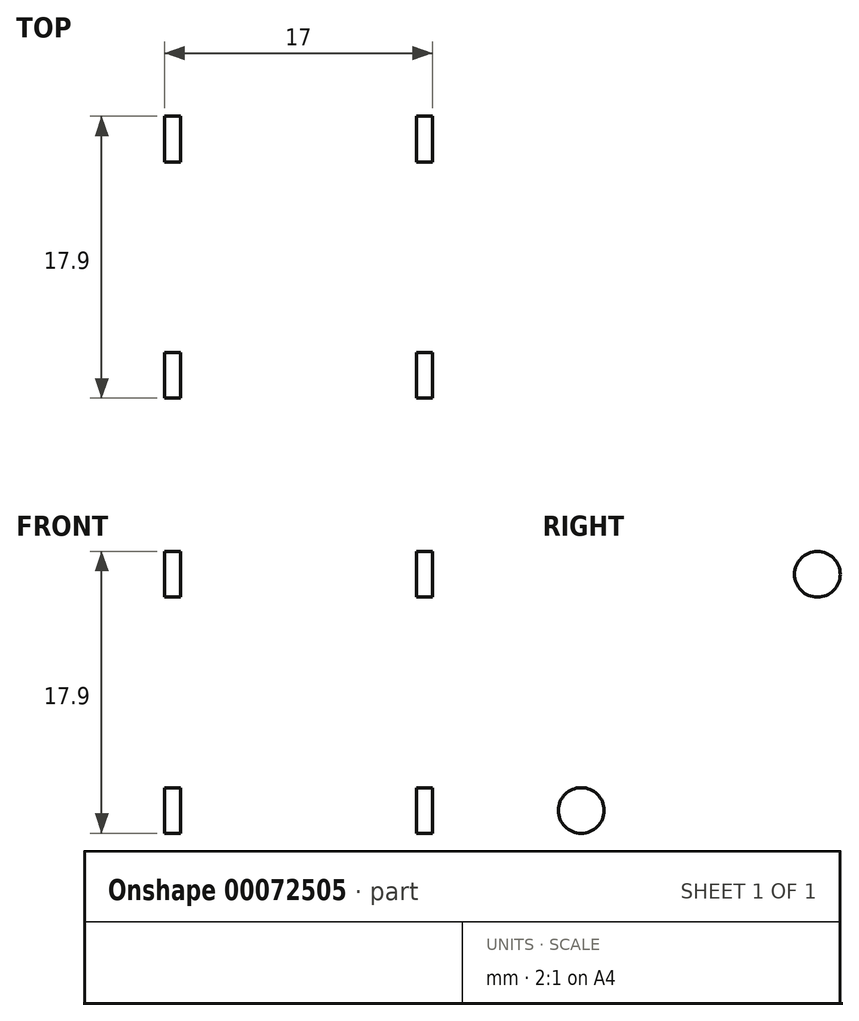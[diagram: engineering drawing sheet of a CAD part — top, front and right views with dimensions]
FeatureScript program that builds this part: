
annotation { "Feature Type Name" : "Feature", "Feature Type Description" : "" }
export const myFeature = defineFeature(function(context is Context, id is Id, definition is map)
    precondition{}
    {
        {
            var Q0;
            Q0=qCreatedBy(makeId("Front.planeOp"),FACE);
            var sketch = newSketch(context, id + "F0", { "sketchPlane" : qUnion([Q0])});
            skLineSegment(sketch, "E0.rect.bottom", {"start": v(-8.5, 25.3) * mm, "end": v(8.5, 25.3) * mm});
            skLineSegment(sketch, "E0.rect.top", {"start": v(-8.5, -25.3) * mm, "end": v(8.5, -25.3) * mm});
            skLineSegment(sketch, "E0.rect.left", {"start": v(-8.5, 25.3) * mm, "end": v(-8.5, -25.3) * mm});
            skLineSegment(sketch, "E0.rect.right", {"start": v(8.5, 25.3) * mm, "end": v(8.5, -25.3) * mm});
            skPoint(sketch, "E0.rect.middle", {"position": v(0, 0) * mm});
            skSolve(sketch);
        }
        {
            var Q0;
            Q0=makeQuery(id+"F0.imprint","IMPRINT",FACE,{"disambiguationData":[TD([[makeQuery(id+"F0.imprint","IMPRINT",EDGE,{"derivedFrom":sQuery(id+"F0.wireOp",EDGE,"E0.rect.bottom")}),-1.0]])]});
            extrude(context, id + "F1", {"entities" : qUnion([Q0]), "depth" : 25 * mm});
        }
        {
            var Q0;
            Q0=makeQuery(id+"F1.opExtrude","SWEPT_FACE",FACE,{"disambiguationData":[OSD([sQuery(id+"F0.wireOp",EDGE,"E0.rect.bottom")])]});
            var Q1;
            Q1=makeQuery(id+"F1.opExtrude","SWEPT_FACE",FACE,{"disambiguationData":[OSD([sQuery(id+"F0.wireOp",EDGE,"E0.rect.top")])]});
            shell(context, id + "F2", {"entities" : qUnion([Q0, Q1]), "thickness" : 1 * mm});
        }
        {
            var Q0;
            Q0=makeQuery(id+"F1.opExtrude","SWEPT_FACE",FACE,{"disambiguationData":[OSD([sQuery(id+"F0.wireOp",EDGE,"E0.rect.right")])]});
            var sketch = newSketch(context, id + "F3", { "sketchPlane" : qUnion([Q0])});
            skLineSegment(sketch, "E1", {"start": v(-12.5, 30.49) * mm, "end": v(-12.5, -29.43) * mm, "construction": true});
            skPoint(sketch, "E1.startSnap0", {"position": v(-12.5, 25.3) * mm});
            skPoint(sketch, "E1.endSnap0", {"position": v(-12.5, -25.3) * mm});
            skLineSegment(sketch, "E2", {"start": v(-31.7, 0) * mm, "end": v(16.22, 0) * mm, "construction": true});
            skPoint(sketch, "E2.startSnap0", {"position": v(-25, 0) * mm});
            skCircle(sketch, "E3", {"center": v(-20, 7.5) * mm, "radius": 1.45 * mm});
            skLineSegment(sketch, "E4.MirrorCS", {"start": v(6.7, 0) * mm, "end": v(-41.22, 0) * mm, "construction": true});
            skCircle(sketch, "E5.MirrorC", {"center": v(-5, 7.5) * mm, "radius": 1.45 * mm});
            skCircle(sketch, "E6.MirrorC", {"center": v(-20, -7.5) * mm, "radius": 1.45 * mm});
            skCircle(sketch, "E7.MirrorC", {"center": v(-5, -7.5) * mm, "radius": 1.45 * mm});
            skSolve(sketch);
        }
        {
            var Q0;
            Q0=makeQuery(id+"F3.imprint","IMPRINT",FACE,{"disambiguationData":[TD([[makeQuery(id+"F3.imprint","IMPRINT",EDGE,{"derivedFrom":sQuery(id+"F3.wireOp",EDGE,"E5.MirrorC")}),-1.0]])]});
            var Q1;
            Q1=makeQuery(id+"F3.imprint","IMPRINT",FACE,{"disambiguationData":[TD([[makeQuery(id+"F3.imprint","IMPRINT",EDGE,{"derivedFrom":sQuery(id+"F3.wireOp",EDGE,"E3")}),1.0]])]});
            var Q2;
            Q2=makeQuery(id+"F3.imprint","IMPRINT",FACE,{"disambiguationData":[TD([[makeQuery(id+"F3.imprint","IMPRINT",EDGE,{"derivedFrom":sQuery(id+"F3.wireOp",EDGE,"E6.MirrorC")}),-1.0]])]});
            var Q3;
            Q3=makeQuery(id+"F3.imprint","IMPRINT",FACE,{"disambiguationData":[TD([[makeQuery(id+"F3.imprint","IMPRINT",EDGE,{"derivedFrom":sQuery(id+"F3.wireOp",EDGE,"E7.MirrorC")}),1.0]])]});
            extrude(context, id + "F4", {"entities" : qUnion([Q0, Q1, Q2, Q3]), "operationType" : NewBodyOperationType.REMOVE, "oppositeDirection" : true, "depth" : 25 * mm});
        }
    });
